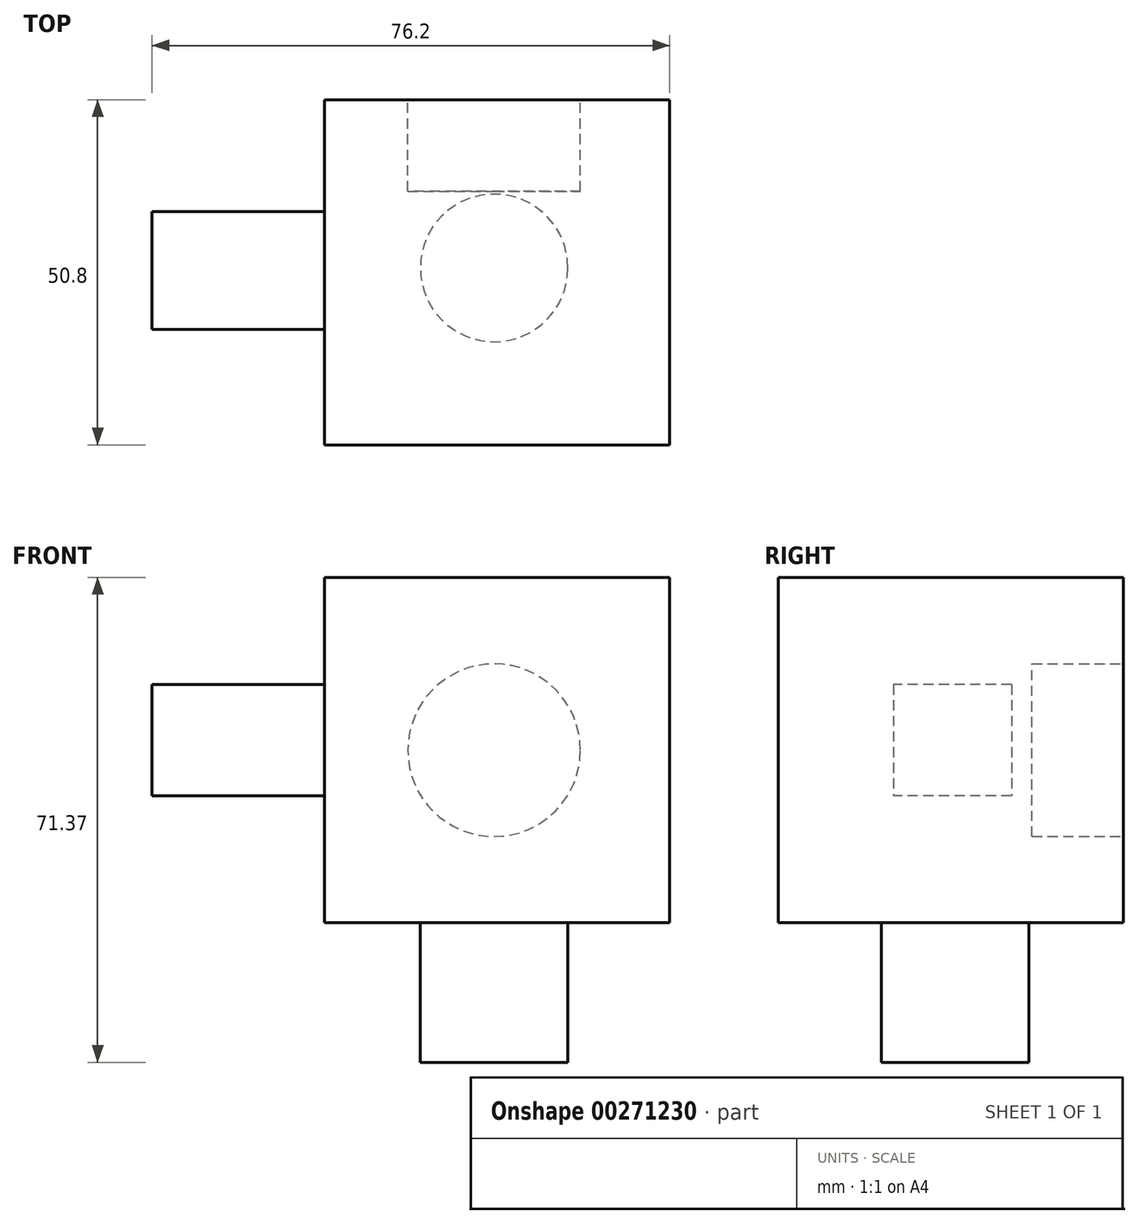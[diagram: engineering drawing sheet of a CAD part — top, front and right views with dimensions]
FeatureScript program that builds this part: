
annotation { "Feature Type Name" : "Feature", "Feature Type Description" : "" }
export const myFeature = defineFeature(function(context is Context, id is Id, definition is map)
    precondition{}
    {
        {
            var Q0;
            Q0=qCreatedBy(makeId("Front.planeOp"),FACE);
            var sketch = newSketch(context, id + "F0", { "sketchPlane" : qUnion([Q0])});
            skLineSegment(sketch, "E0.bottom", {"start": v(0, 0) * mm, "end": v(50.8, 0) * mm});
            skLineSegment(sketch, "E0.top", {"start": v(0, 50.8) * mm, "end": v(50.8, 50.8) * mm});
            skLineSegment(sketch, "E0.left", {"start": v(0, 0) * mm, "end": v(0, 50.8) * mm});
            skLineSegment(sketch, "E0.right", {"start": v(50.8, 0) * mm, "end": v(50.8, 50.8) * mm});
            skSolve(sketch);
        }
        {
            var Q0;
            Q0=makeQuery(id+"F0.imprint","IMPRINT",FACE,{"disambiguationData":[TD([[makeQuery(id+"F0.imprint","IMPRINT",EDGE,{"derivedFrom":sQuery(id+"F0.wireOp",EDGE,"E0.bottom")}),1.0]])]});
            extrude(context, id + "F1", {"entities" : qUnion([Q0]), "depth" : 50.8 * mm});
        }
        {
            var Q0;
            Q0=qCreatedBy(makeId("Front.planeOp"),FACE);
            var sketch = newSketch(context, id + "F2", { "sketchPlane" : qUnion([Q0])});
            skCircle(sketch, "E1", {"center": v(24.96, 25.35) * mm, "radius": 12.7 * mm});
            skSolve(sketch);
        }
        {
            var Q0;
            Q0=makeQuery(id+"F2.imprint","IMPRINT",FACE,{"disambiguationData":[TD([[makeQuery(id+"F2.imprint","IMPRINT",EDGE,{"derivedFrom":sQuery(id+"F2.wireOp",EDGE,"E1")}),1.0]])]});
            extrude(context, id + "F3", {"entities" : qUnion([Q0]), "operationType" : NewBodyOperationType.REMOVE, "depth" : 13.46 * mm});
        }
        {
            var Q0;
            Q0=qCreatedBy(makeId("Top.planeOp"),FACE);
            var sketch = newSketch(context, id + "F4", { "sketchPlane" : qUnion([Q0])});
            skCircle(sketch, "E2", {"center": v(24.96, -24.76) * mm, "radius": 10.86 * mm});
            skSolve(sketch);
        }
        {
            var Q0;
            Q0=makeQuery(id+"F4.imprint","IMPRINT",FACE,{"disambiguationData":[TD([[makeQuery(id+"F4.imprint","IMPRINT",EDGE,{"derivedFrom":sQuery(id+"F4.wireOp",EDGE,"E2")}),1.0]])]});
            extrude(context, id + "F5", {"entities" : qUnion([Q0]), "operationType" : NewBodyOperationType.ADD, "oppositeDirection" : true, "depth" : 20.57 * mm});
        }
        {
            var Q0;
            Q0=makeQuery(id+"F1.opExtrude","SWEPT_FACE",FACE,{"disambiguationData":[OSD([sQuery(id+"F0.wireOp",EDGE,"E0.left")])]});
            var sketch = newSketch(context, id + "F6", { "sketchPlane" : qUnion([Q0])});
            skLineSegment(sketch, "E3.bottom", {"start": v(16.48, 35.02) * mm, "end": v(33.84, 35.02) * mm});
            skLineSegment(sketch, "E3.top", {"start": v(16.48, 18.65) * mm, "end": v(33.84, 18.65) * mm});
            skLineSegment(sketch, "E3.left", {"start": v(16.48, 35.02) * mm, "end": v(16.48, 18.65) * mm});
            skLineSegment(sketch, "E3.right", {"start": v(33.84, 35.02) * mm, "end": v(33.84, 18.65) * mm});
            skSolve(sketch);
        }
        {
            var Q0;
            Q0=makeQuery(id+"F6.imprint","IMPRINT",FACE,{"disambiguationData":[TD([[makeQuery(id+"F6.imprint","IMPRINT",EDGE,{"derivedFrom":sQuery(id+"F6.wireOp",EDGE,"E3.bottom")}),-1.0]])]});
            extrude(context, id + "F7", {"entities" : qUnion([Q0]), "operationType" : NewBodyOperationType.ADD, "depth" : 25.4 * mm});
        }
    });
